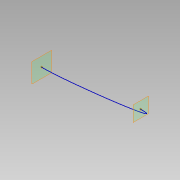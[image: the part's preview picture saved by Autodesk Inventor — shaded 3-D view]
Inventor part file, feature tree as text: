
AUTODESK INVENTOR PART (.ipt)
format: ipt  version: 2019 (Build 230136000, 136)  size: 88,576 bytes
history: native  units: mm
features: other x2, plane x2, sketch x1
ambient origin geometry x8: Origin, YZ Plane, XZ Plane, XY Plane, X Axis, Y Axis, Z Axis, Center Point
feature tree (5):
  other  "Punto de trabajo1"
  other  "Punto de trabajo2"
  plane  "Plano de trabajo1"
  plane  "Plano de trabajo2"
  sketch  "Boceto 3D1"  dims[d0=10.0mm d1=-0.1mm d2=-10.0mm d3=-0.1mm]
